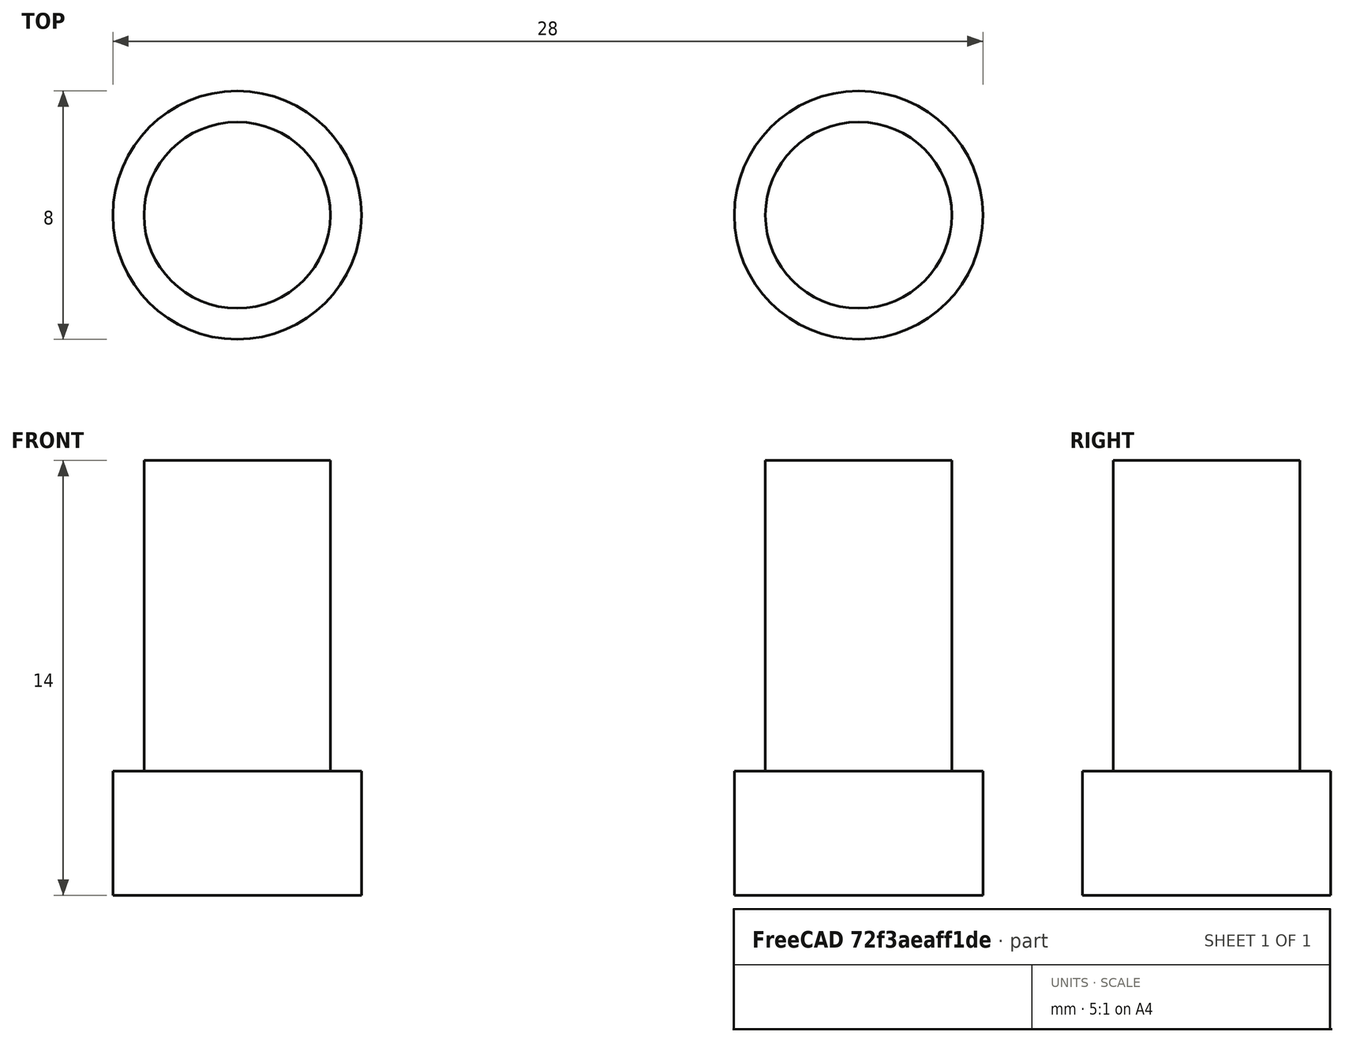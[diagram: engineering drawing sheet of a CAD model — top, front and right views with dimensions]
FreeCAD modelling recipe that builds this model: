
FCSTD DOCUMENT  (FreeCAD 0.18R4 (GitTag))
Label: DragonMMCButtons-v3
License: All rights reserved
LicenseURL: http://en.wikipedia.org/wiki/All_rights_reserved
objects: Part::Cylinder×2, Part::FeaturePython×2, Part::MultiFuse×1
note: 5 computed .brp shape members not serialized (recipe doc carries the construction recipe); baked Part::Feature solids carry a one-line shape summary decoded from their .brp

FEATURE [Part::Cylinder] Cylinder  label="Lower cylinder"
  Angle = 360
  AttacherType = Attacher::AttachEngine3D
  Height = 4
  Radius = 4
FEATURE [Part::Cylinder] Cylinder001  label="Upper cylinder"
  Angle = 360
  AttacherType = Attacher::AttachEngine3D
  Height = 10
  Placement = pos=(0,0,4) rot=(0,0,1;0rad)
  Radius = 3
FEATURE [Part::MultiFuse] Fusion  label="Button 1"
  Shapes = -> [Cylinder001,Cylinder]
FEATURE [Part::FeaturePython] Clone  label="Button 2"  # Draft clone (typed FeaturePython)
  AttacherType = Attacher::AttachEngine3D
  Fuse = false
  Objects = -> [Fusion]
  Placement = pos=(20,0,0) rot=(0,0,1;0rad)
  Scale = (1,1,1)
FEATURE [Part::FeaturePython] Clone001  label="Button 3"  # Draft clone (typed FeaturePython)
  AttacherType = Attacher::AttachEngine3D
  Fuse = false
  Objects = -> [Fusion]
  Placement = pos=(40,0,0) rot=(0,0,1;0rad)
  Scale = (1,1,1)
